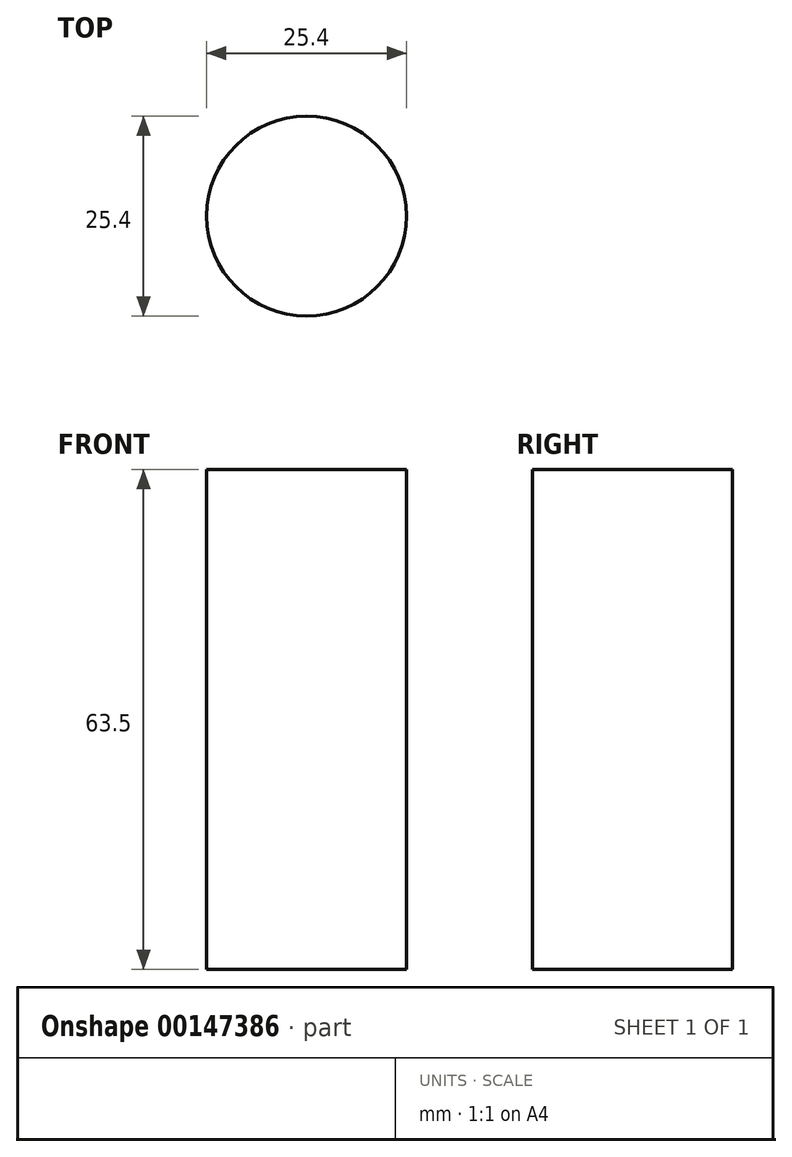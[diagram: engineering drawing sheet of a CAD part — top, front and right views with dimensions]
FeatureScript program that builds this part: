
annotation { "Feature Type Name" : "Feature", "Feature Type Description" : "" }
export const myFeature = defineFeature(function(context is Context, id is Id, definition is map)
    precondition{}
    {
        {
            var Q0;
            Q0=qCreatedBy(makeId("Top.planeOp"),FACE);
            var sketch = newSketch(context, id + "F0", { "sketchPlane" : qUnion([Q0])});
            skCircle(sketch, "E0", {"center": v(0, 0) * mm, "radius": 12.7 * mm});
            skSolve(sketch);
        }
        {
            var Q0;
            Q0 = qSketchRegion(id + "F0", true);
            extrude(context, id + "F1", {"entities" : qUnion([Q0]), "endBound" : BoundingType.SYMMETRIC, "depth" : 63.5 * mm});
        }
    });
